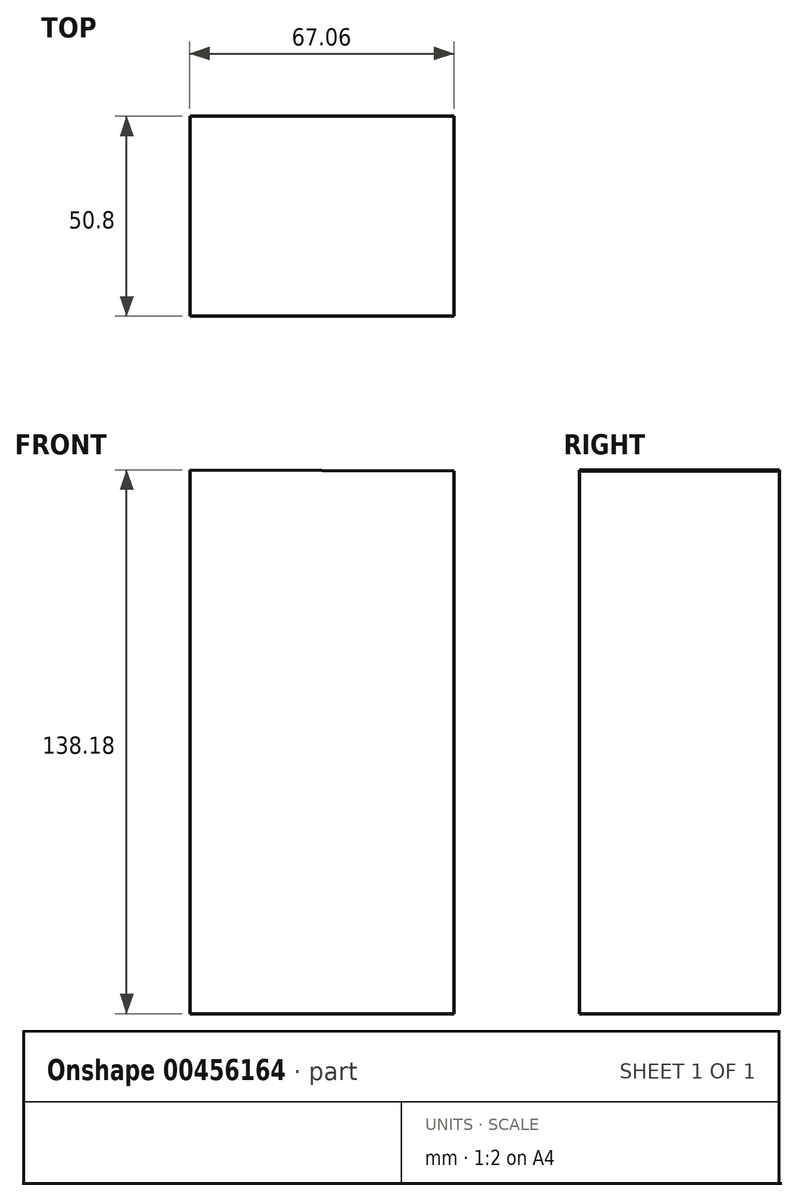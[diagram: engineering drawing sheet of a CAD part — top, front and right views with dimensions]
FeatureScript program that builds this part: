
annotation { "Feature Type Name" : "Feature", "Feature Type Description" : "" }
export const myFeature = defineFeature(function(context is Context, id is Id, definition is map)
    precondition{}
    {
        {
            var Q0;
            Q0=qCreatedBy(makeId("Front.planeOp"),FACE);
            var sketch = newSketch(context, id + "F0", { "sketchPlane" : qUnion([Q0])});
            skLineSegment(sketch, "E0", {"start": v(-67.06, 138.18) * mm, "end": v(-67.06, 0) * mm});
            skLineSegment(sketch, "E1", {"start": v(-67.06, 0) * mm, "end": v(0, 0) * mm});
            skLineSegment(sketch, "E2", {"start": v(0, 0) * mm, "end": v(0, 137.82) * mm});
            skLineSegment(sketch, "E3", {"start": v(0, 137.82) * mm, "end": v(-67.06, 138.18) * mm});
            skSolve(sketch);
        }
        {
            var Q0;
            Q0 = qSketchRegion(id + "F0", true);
            extrude(context, id + "F1", {"entities" : qUnion([Q0]), "depth" : 50.8 * mm});
        }
    });
